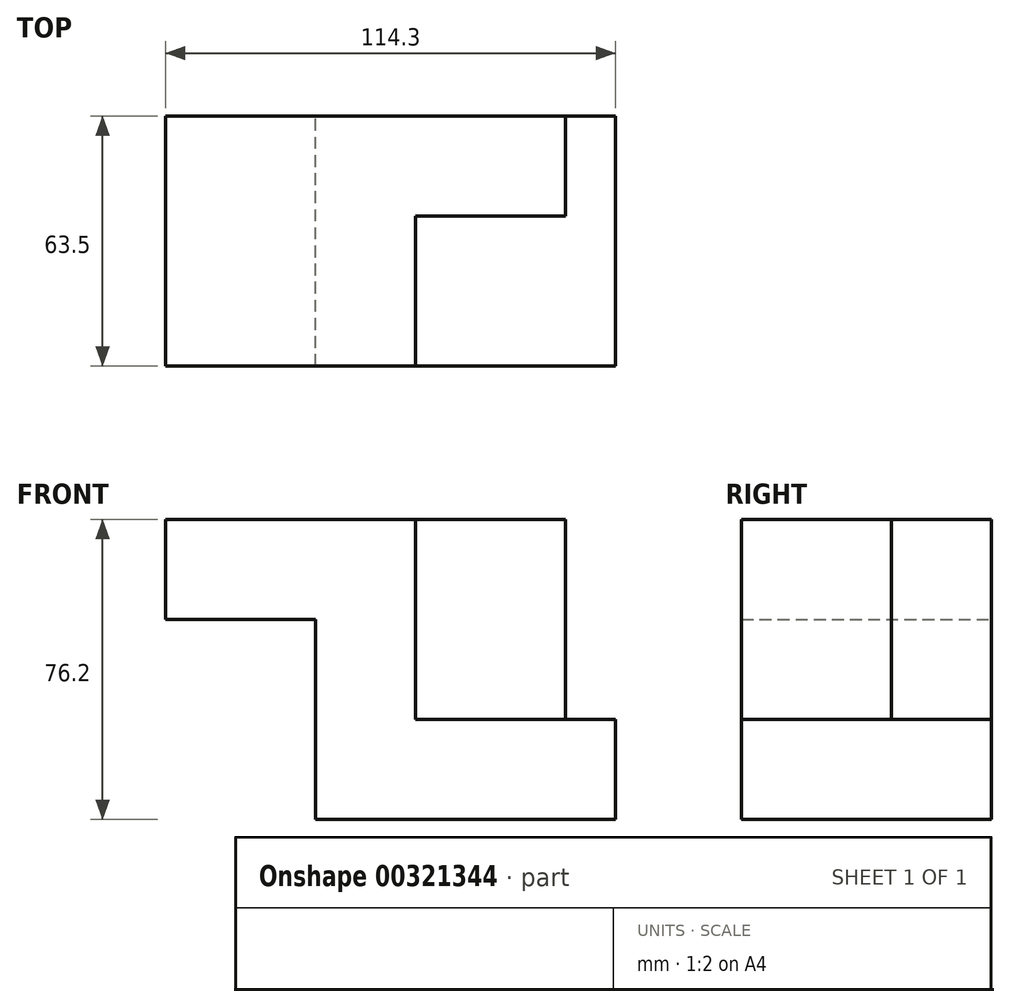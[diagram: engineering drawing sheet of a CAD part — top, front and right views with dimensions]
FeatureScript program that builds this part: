
annotation { "Feature Type Name" : "Feature", "Feature Type Description" : "" }
export const myFeature = defineFeature(function(context is Context, id is Id, definition is map)
    precondition{}
    {
        {
            var Q0;
            Q0=qCreatedBy(makeId("Front.planeOp"),FACE);
            var sketch = newSketch(context, id + "F0", { "sketchPlane" : qUnion([Q0])});
            skLineSegment(sketch, "E0", {"start": v(-82.8, 69.75) * mm, "end": v(-19.3, 69.75) * mm});
            skLineSegment(sketch, "E1", {"start": v(-19.3, 69.75) * mm, "end": v(-19.3, 18.95) * mm});
            skLineSegment(sketch, "E2", {"start": v(-19.3, 18.95) * mm, "end": v(31.5, 18.95) * mm});
            skLineSegment(sketch, "E3", {"start": v(31.5, 18.95) * mm, "end": v(31.5, -6.45) * mm});
            skLineSegment(sketch, "E4", {"start": v(31.5, -6.45) * mm, "end": v(-44.7, -6.45) * mm});
            skLineSegment(sketch, "E5", {"start": v(-44.7, -6.45) * mm, "end": v(-44.7, 44.35) * mm});
            skLineSegment(sketch, "E6", {"start": v(-44.7, 44.35) * mm, "end": v(-82.8, 44.35) * mm});
            skLineSegment(sketch, "E7", {"start": v(-82.8, 44.35) * mm, "end": v(-82.8, 69.75) * mm});
            skSolve(sketch);
        }
        {
            var Q0;
            Q0=makeQuery(id+"F0.imprint","IMPRINT",FACE,{"disambiguationData":[TD([[makeQuery(id+"F0.imprint","IMPRINT",EDGE,{"derivedFrom":sQuery(id+"F0.wireOp",EDGE,"E0")}),-1.0]])]});
            extrude(context, id + "F1", {"entities" : qUnion([Q0]), "depth" : 63.5 * mm});
        }
        {
            var Q0;
            Q0=makeQuery(id+"F1.opExtrude","SWEPT_FACE",FACE,{"disambiguationData":[OSD([sQuery(id+"F0.wireOp",EDGE,"E2")])]});
            var sketch = newSketch(context, id + "F2", { "sketchPlane" : qUnion([Q0])});
            skLineSegment(sketch, "E8", {"start": v(-19.3, -25.4) * mm, "end": v(18.8, -25.4) * mm});
            skLineSegment(sketch, "E9", {"start": v(18.8, -25.4) * mm, "end": v(18.8, 0) * mm});
            skSolve(sketch);
        }
        {
            var Q0;
            Q0 = qSketchRegion(id + "F2", true);
            var Q1;
            {var subQ0=sQuery(id+"F2.wireOp",EDGE,"E8");Q1=makeQuery(id+"F2.imprint","IMPRINT",FACE,{"disambiguationData":[TD([[makeQuery(id+"F2.imprint","IMPRINT",EDGE,{"derivedFrom":subQ0}),1.0]])]});}
            extrude(context, id + "F3", {"entities" : qUnion([Q0, Q1]), "operationType" : NewBodyOperationType.ADD, "depth" : 50.8 * mm});
        }
    });
